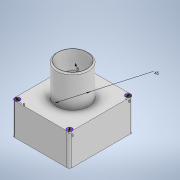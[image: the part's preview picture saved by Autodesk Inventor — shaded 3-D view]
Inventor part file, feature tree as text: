
AUTODESK INVENTOR PART (.ipt)
format: ipt  version: 2022 (Build 260153000, 153)  size: 171,008 bytes
history: native  units: mm
features: sketch x8, hole x4, thread x4, extrude x3, fillet x2, chamfer x1
ambient origin geometry x8: Origin, YZ Plane, XZ Plane, XY Plane, X Axis, Y Axis, Z Axis, Center Point
bodies: Solid1 (feature_tree)
feature tree (22):
  extrude  "Extrusion1"  Depth=100.0mm
  extrude  "Extrusion2"  Depth=50.0mm
  sketch  "Sketch3"  dims[d9=4.0mm d16=45.0mm]
  fillet  "Fillet1"  Radius=50.0mm
  fillet  "Fillet2"  Radius=4.0mm
  sketch  "Sketch4"  dims[d17=45.0mm d18=30.0mm d19=0.0mm]
  sketch  "Sketch5"  dims[d20=8.0mm d21=8.0mm]
  extrude  "Extrusion3"  Depth=4.0mm
  sketch  "Sketch7"  dims[d24=8.0mm d25=6.0mm d26=4.0mm d27=2.0mm d28=90.0deg d29=8.0mm d30=20.594885mm]
  sketch  "Sketch8"  dims[d31=8.0mm d32=6.0mm d33=4.0mm d34=2.0mm d35=90.0deg d36=8.0mm d37=20.594885mm d38=8.0mm d39=6.0mm d40=4.0mm d41=2.0mm d42=90.0deg d43=8.0mm d44=20.594885mm d45=8.0mm d46=6.0mm d47=4.0mm d48=2.0mm d49=90.0deg d50=8.0mm d51=20.594885mm d52=50.0mm d53=0.0mm d54=50.0mm d55=0.0mm d56=50.0mm d57=0.0mm d58=50.0mm d59=0.0mm d60=2.0mm d61=2.0mm d62=45.0deg d63=0.375mm]
  hole  "Hole1"  [1 undecoded]
  hole  "Hole2"  [1 undecoded]
  hole  "Hole3"  [1 undecoded]
  hole  "Hole4"  [1 undecoded]
  thread  "Thread1"  [1 undecoded]
  thread  "Thread2"  [1 undecoded]
  thread  "Thread3"  [1 undecoded]
  thread  "Thread4"  [1 undecoded]
  chamfer  "Chamfer1"  Distance=0.375mm
  sketch  "Sketch1"  dims[d0=90.0mm d1=100.0mm]
  sketch  "Sketch2"  dims[d3=50.0mm d4=0.0mm d5=50.0mm d6=50.0mm d7=0.0mm d8=4.0mm]
  sketch  "Sketch6"  dims[d22=8.0mm d23=8.0mm]
note: 8 required parameter values undecoded (feature->parameter linkage not recoverable at this tier; creation-order binding heuristic only, values carry confidence <= 0.55)
